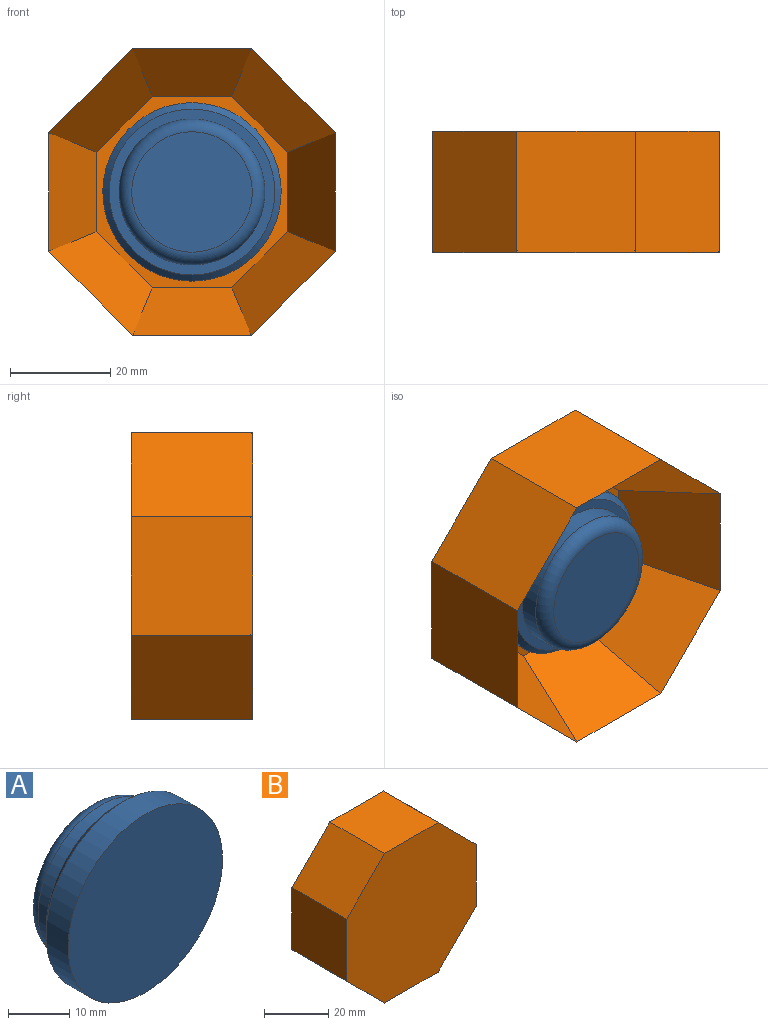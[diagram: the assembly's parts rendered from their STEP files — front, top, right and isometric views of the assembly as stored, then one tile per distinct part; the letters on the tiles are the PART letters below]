
ASSEMBLY  parts=2 mates=1
PART A: 7 faces, bbox 35.6x12.7x35.6 mm
  f0: cylinder r=17.78mm len=35.56mm, axis (0,-1,0), area 567.5mm2, adj f2,f6
  f1: plane 33.02x33.02mm, normal (0,1,0), area 191.6mm2, adj f3,f6
  f2: plane 35.56x35.56mm, normal (0,-1,0), area 993.1mm2, adj f0
  f3: cylinder r=14.55mm len=29.09mm, axis (0,-1,0), area 348.2mm2, adj f1,f5
  f4: plane 24.01x24.01mm, normal (0,1,0), area 452.9mm2, adj f5
  f5: torus R=12.01mm, axis (0,-1,0), area 341.5mm2, adj f3,f4
  f6: cone r=17.78mm half-angle=45deg, axis (0,-1,0), area 193.5mm2, adj f0,f1
PART B: 22 faces, bbox 57.2x24.1x57.2 mm
  f0: plane 24.13x16.74mm, normal (-0.71,0,-0.71), area 571.2mm2, adj f1,f7,f8,f15
  f1: plane 24.13x23.67mm, normal (0,0,-1), area 571.2mm2, adj f0,f2,f8,f17
  f2: plane 24.13x16.74mm, normal (0.71,0,-0.71), area 571.2mm2, adj f1,f3,f8,f16
  f3: plane 24.13x23.67mm, normal (1,0,0), area 571.2mm2, adj f2,f4,f8,f14
  f4: plane 24.13x16.74mm, normal (0.71,0,0.71), area 571.2mm2, adj f3,f5,f8,f12
  f5: plane 24.13x23.67mm, normal (0,0,1), area 571.2mm2, adj f4,f6,f8,f10
  f6: plane 24.13x16.74mm, normal (-0.71,0,0.71), area 571.2mm2, adj f5,f7,f8,f11
  f7: plane 24.13x23.67mm, normal (-1,0,0), area 571.2mm2, adj f0,f6,f8,f13
  f8: plane 57.15x57.15mm, normal (0,-1,0), area 2705.7mm2, adj f0,f1,f2,f3,f4,f5,f6,f7
  f9: plane 38.1x38.1mm, normal (0,1,0), area 1139.2mm2, adj f10,f11,f12,f13,f14,f15,f16,f17
  f10: plane 23.67x19.05mm, normal (0,0.45,-0.89), area 420.2mm2, adj f5,f9,f11,f12
  f11: plane 20.68x20.68mm, normal (0.63,0.45,-0.63), area 420.2mm2, adj f6,f9,f10,f13
  f12: plane 20.68x20.68mm, normal (-0.63,0.45,-0.63), area 420.2mm2, adj f4,f9,f10,f14
  f13: plane 23.67x19.05mm, normal (0.89,0.45,0), area 420.2mm2, adj f7,f9,f11,f15
  f14: plane 23.67x19.05mm, normal (-0.89,0.45,0), area 420.2mm2, adj f3,f9,f12,f16
  f15: plane 20.68x20.68mm, normal (0.63,0.45,0.63), area 420.2mm2, adj f0,f9,f13,f17
  f16: plane 20.68x20.68mm, normal (-0.63,0.45,0.63), area 420.2mm2, adj f2,f9,f14,f17
  f17: plane 23.67x19.05mm, normal (0,0.45,0.89), area 420.2mm2, adj f1,f9,f15,f16
  f18: cylinder r=3.17mm len=6.35mm, axis (0,-1,0), area 63.3mm2, adj f9,f19
  f19: plane 6.35x6.35mm, normal (0,1,0), area 31.7mm2, adj f18
  f20: cylinder r=3.17mm len=6.35mm, axis (0,-1,0), area 63.3mm2, adj f9,f21
  f21: plane 6.35x6.35mm, normal (0,1,0), area 31.7mm2, adj f20
PLACE A rot(axis=(0,0,-1),180deg) t=(-0.92,15.34,-1.25)mm
PLACE B rot(axis=(0,0,-1),180deg) t=(-0.74,-3.71,-1.25)mm
MATE fastened B.f9 <-> A.f0  axis (0,-1,0) through (-0.74,15.34,-1.25)mm
